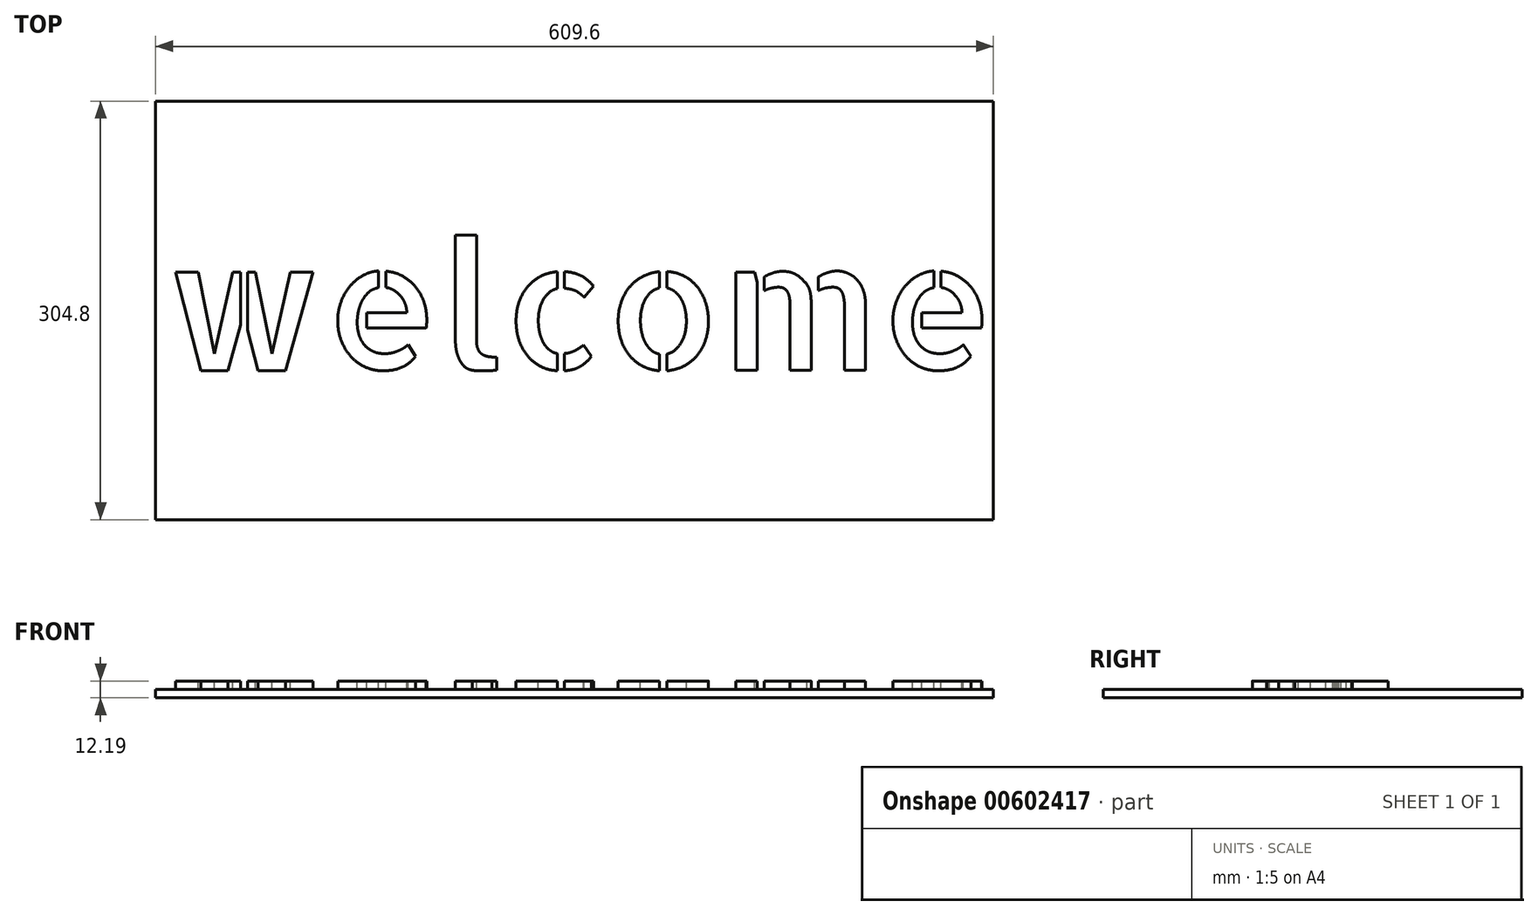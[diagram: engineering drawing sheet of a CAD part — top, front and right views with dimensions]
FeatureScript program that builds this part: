
annotation { "Feature Type Name" : "Feature", "Feature Type Description" : "" }
export const myFeature = defineFeature(function(context is Context, id is Id, definition is map)
    precondition{}
    {
        {
            var Q0;
            Q0=qCreatedBy(makeId("Top.planeOp"),FACE);
            var sketch = newSketch(context, id + "F0", { "sketchPlane" : qUnion([Q0])});
            skLineSegment(sketch, "E0.bottom", {"start": v(0, 0) * mm, "end": v(609.6, 0) * mm});
            skLineSegment(sketch, "E0.top", {"start": v(0, -304.8) * mm, "end": v(609.6, -304.8) * mm});
            skLineSegment(sketch, "E0.left", {"start": v(0, 0) * mm, "end": v(0, -304.8) * mm});
            skLineSegment(sketch, "E0.right", {"start": v(609.6, 0) * mm, "end": v(609.6, -304.8) * mm});
            skSolve(sketch);
        }
        {
            var Q0;
            Q0=makeQuery(id+"F0.imprint","IMPRINT",FACE,{"disambiguationData":[TD([[makeQuery(id+"F0.imprint","IMPRINT",EDGE,{"derivedFrom":sQuery(id+"F0.wireOp",EDGE,"E0.bottom")}),-1.0]])]});
            extrude(context, id + "F1", {"entities" : qUnion([Q0]), "depth" : 12.2 * mm, "offsetDistance" : 30.48 * mm});
        }
        {
            var Q0;
            Q0=makeQuery(id+"F1.opExtrude","CAP_FACE",FACE,{"disambiguationData":[OSD([sQuery(id+"F0.wireOp",EDGE,"E0.bottom"),sQuery(id+"F0.wireOp",EDGE,"E0.top"),sQuery(id+"F0.wireOp",EDGE,"E0.left"),sQuery(id+"F0.wireOp",EDGE,"E0.right")])],"isStart":false});
            var sketch = newSketch(context, id + "F2", { "sketchPlane" : qUnion([Q0])});
            skText(sketch, "E1", { "text": "welcome", "fontName": "AllertaStencil-Regular.ttf"});
            const initialGuessF2  = {"E1": [0.00539, -0.19585, 1, 0, 0.09334]};
            skSetInitialGuess(sketch, initialGuessF2);
            skSolve(sketch);
        }
        {
            var Q0;
            Q0=makeQuery(id+"F2.imprint","IMPRINT",FACE,{"disambiguationData":[TD([[makeQuery(id+"F2.imprint","IMPRINT",EDGE,{"derivedFrom":sQuery(id+"F2.wireOp",EDGE,"E1.sketch_text.stroke-0")}),1.0]])]});
            extrude(context, id + "F3", {"entities" : qUnion([Q0]), "operationType" : NewBodyOperationType.REMOVE, "oppositeDirection" : true, "depth" : 6.1 * mm, "offsetDistance" : 30.48 * mm});
        }
    });
